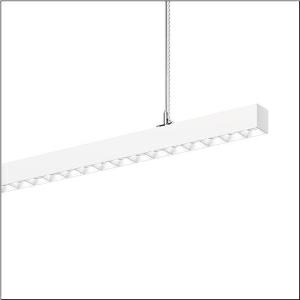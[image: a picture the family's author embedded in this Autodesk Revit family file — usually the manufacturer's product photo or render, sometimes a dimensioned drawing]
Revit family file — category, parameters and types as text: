
# Revit family: silica_r__21_51mx35da47wb_183f
name_source: partatom
category: Lighting Fixtures
units: mm (PartAtom-declared; Revit-internal decimal feet)

## family parameters
Cut with Voids When Loaded = No
Host = Face
Light Source = No
Part Type = Normal
Room Calculation Point = No
Round Connector Dimension = Use Diameter
Shared = No

## types (1)
- --- (1 x LED, 7080 lm, 40.6 W, 4000K)
    Apparent Load = 41 VA
    CIE Flux Codes = 84 98 100 61 100
    Color Rendering = 80
    Color Temperature = 4000K
    Default Elevation = 1800 mm
    Description = Silica® 21, office luminaire, primary light control with darklight reflector, of PMMA, white, CAT 2 (L<= 3000cd/m²), light emission: direct/indirect distribution, primary light characteristic: symmetric, installation type: suspended mounting, LED, rated luminous flux: 7.080lm, luminous efficacy: 174lm/W, light colour: 840, colour temperature: 4000K, with terminal, 3+2-pole, max. 2.5mm², mains connection: 220..240V, AC, 50/60Hz, rated input power: 40.6W, luminaire housing, of aluminium, traffic white (RAL 9016), length: 1.204mm, width: 53mm, height: 53mm, protection rating (complete): IP20, insulation class (complete): insulation class I (protective earthing), certification: CE, permissible operating ambient temperature: 0..+35°C, standard: EN 50419, packaging unit: 1 piece
    Height = 53 mm
    Lamp = 1 x LED
    Lamp Light Flux = 7080 lm
    Lamp Power = 40.6 W
    Lamp count = 1
    Length = 1204 mm
    Luminous efficacy = 174 lm/W
    Manufacturer = Siteco
    ModVariant = No
    Model = 51MX35DA47WB
    Mounting Place = Ceiling
    Mounting Type = Pendant
    Number of Poles = 1
    OnlyDefault = Yes
    Power Factor = 1
    Product Name = Silica® 21
    Product group = office luminaire | ceiling pendant
    ProductGroupID = 902
    Protection Class = Protection class I
    Protection Degree = IP 20
    RLX_Detail_Level = 1
    RLX_Emergency_Light_Flux = 0 lm
    RLX_Emergency_Type = 0
    RLX_Emergency_Type_DB = No
    RlxData = <blob elided: 41105 chars, md5=3fb23763>
    Socket = socket
    Standby Power = 0 W
    System Light Flux = 7080 lm
    System Power = 41 W
    Type Comments = factory setting: luminous flux: 100 % | dim-lin: 254 | 339 mA
    Type Image = l_1335921.jpg
    URL = http://relux.com
    VarID = @adj_090017
    Voltage = 0 V
    Weight = 0.00 kg
    Width = 53 mm

## geometry (parser evidence)
native form markers: Blend x4, Sweep x12
no freeform markers — native parametric forms only
